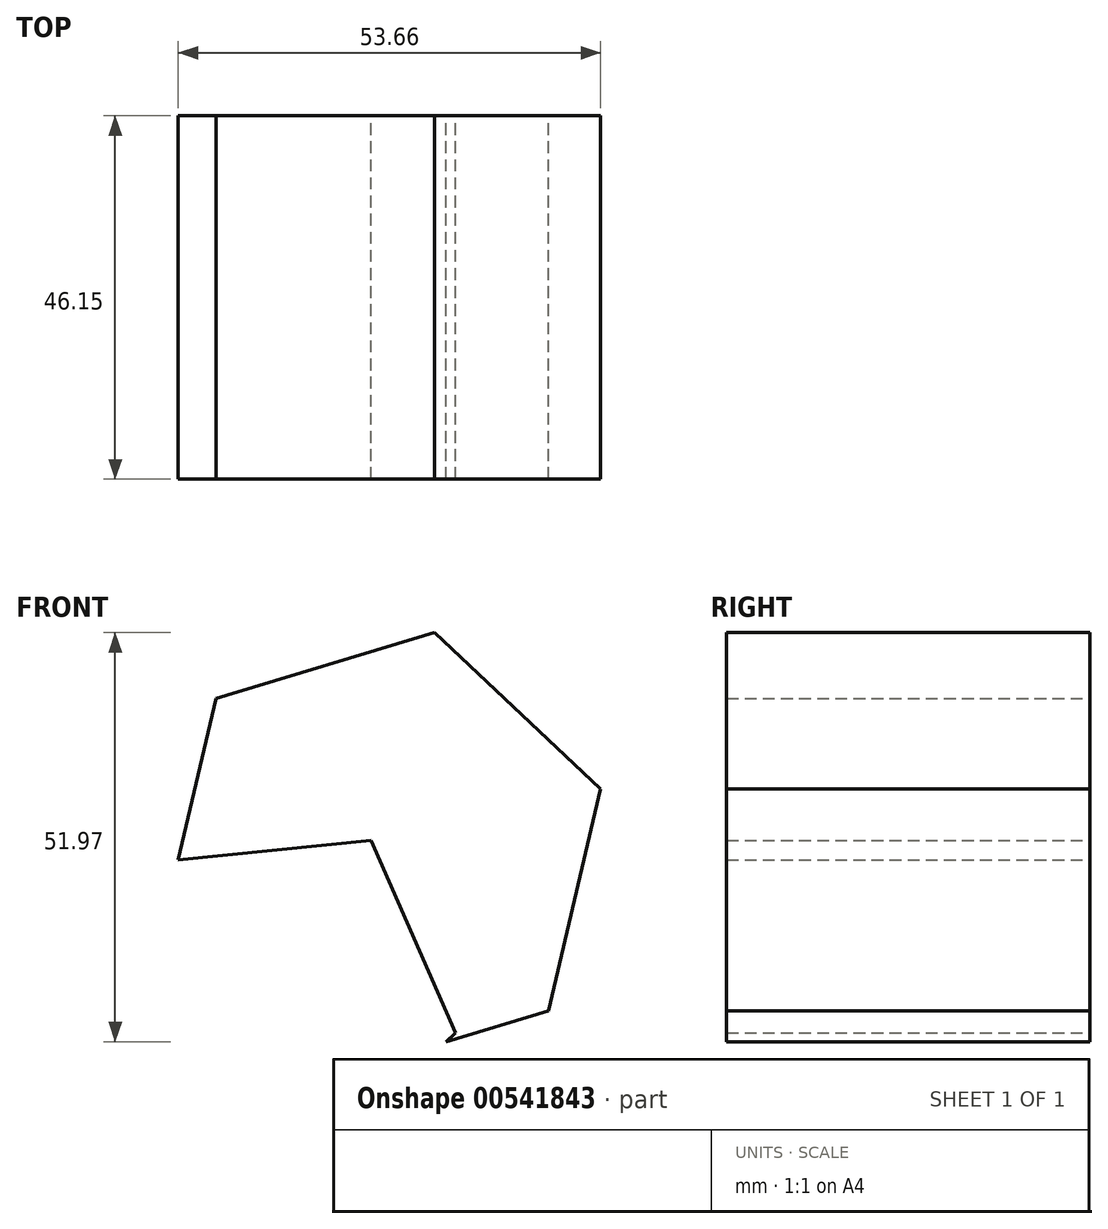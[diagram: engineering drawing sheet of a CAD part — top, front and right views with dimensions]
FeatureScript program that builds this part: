
annotation { "Feature Type Name" : "Feature", "Feature Type Description" : "" }
export const myFeature = defineFeature(function(context is Context, id is Id, definition is map)
    precondition{}
    {
        {
            var Q0;
            Q0=qCreatedBy(makeId("Right.planeOp"),FACE);
            var sketch = newSketch(context, id + "F0", { "sketchPlane" : qUnion([Q0])});
            skSolve(sketch);
        }
        {
            var Q0;
            Q0=qCreatedBy(makeId("Front.planeOp"),FACE);
            var sketch = newSketch(context, id + "F1", { "sketchPlane" : qUnion([Q0])});
            skCircle(sketch, "E0.cCircle", {"center": v(-19.24, 12.9) * mm, "radius": 22.72 * mm, "construction": true});
            skLineSegment(sketch, "E0.0", {"start": v(-16.96, -9.7) * mm, "end": v(-40.04, 3.76) * mm});
            skLineSegment(sketch, "E0.1", {"start": v(-40.04, 3.76) * mm, "end": v(-34.37, 29.85) * mm});
            skLineSegment(sketch, "E0.2", {"start": v(-34.37, 29.85) * mm, "end": v(-7.8, 32.53) * mm});
            skLineSegment(sketch, "E0.3", {"start": v(-7.8, 32.53) * mm, "end": v(2.96, 8.1) * mm});
            skLineSegment(sketch, "E0.4", {"start": v(2.96, 8.1) * mm, "end": v(-16.96, -9.7) * mm});
            skCircle(sketch, "E1.cCircle", {"center": v(0, -9.7) * mm, "radius": 9.7 * mm, "construction": true});
            skLineSegment(sketch, "E1.0", {"start": v(0, 0) * mm, "end": v(9.22, -6.7) * mm});
            skLineSegment(sketch, "E1.1", {"start": v(9.22, -6.7) * mm, "end": v(5.7, -17.54) * mm});
            skLineSegment(sketch, "E1.2", {"start": v(5.7, -17.54) * mm, "end": v(-5.7, -17.54) * mm});
            skLineSegment(sketch, "E1.3", {"start": v(-5.7, -17.54) * mm, "end": v(-9.22, -6.7) * mm});
            skLineSegment(sketch, "E1.4", {"start": v(-9.22, -6.7) * mm, "end": v(0, 0) * mm});
            skCircle(sketch, "E2.cCircle", {"center": v(-6.33, 30.76) * mm, "radius": 28.96 * mm, "construction": true});
            skLineSegment(sketch, "E2.0", {"start": v(21.4, 39.12) * mm, "end": v(14.78, 10.93) * mm});
            skLineSegment(sketch, "E2.1", {"start": v(14.78, 10.93) * mm, "end": v(-12.96, 2.57) * mm});
            skLineSegment(sketch, "E2.2", {"start": v(-12.96, 2.57) * mm, "end": v(-34.06, 22.4) * mm});
            skLineSegment(sketch, "E2.3", {"start": v(-34.06, 22.4) * mm, "end": v(-27.43, 50.6) * mm});
            skLineSegment(sketch, "E2.4", {"start": v(-27.43, 50.6) * mm, "end": v(0.3, 58.96) * mm});
            skLineSegment(sketch, "E2.5", {"start": v(0.3, 58.96) * mm, "end": v(21.4, 39.12) * mm});
            skSolve(sketch);
        }
        {
            var Q0;
            {var subQ2=sQuery(id+"F1.wireOp",EDGE,"E0.3");Q0=makeQuery(id+"F1.imprint","IMPRINT",FACE,{"disambiguationData":[TD([[makeQuery(id+"F1.imprint","IMPRINT",EDGE,{"derivedFrom":subQ2}),1.0]])]});}
            extrude(context, id + "F2", {"entities" : qUnion([Q0]), "depth" : 46.15 * mm, "offsetDistance" : 25 * mm});
        }
    });
